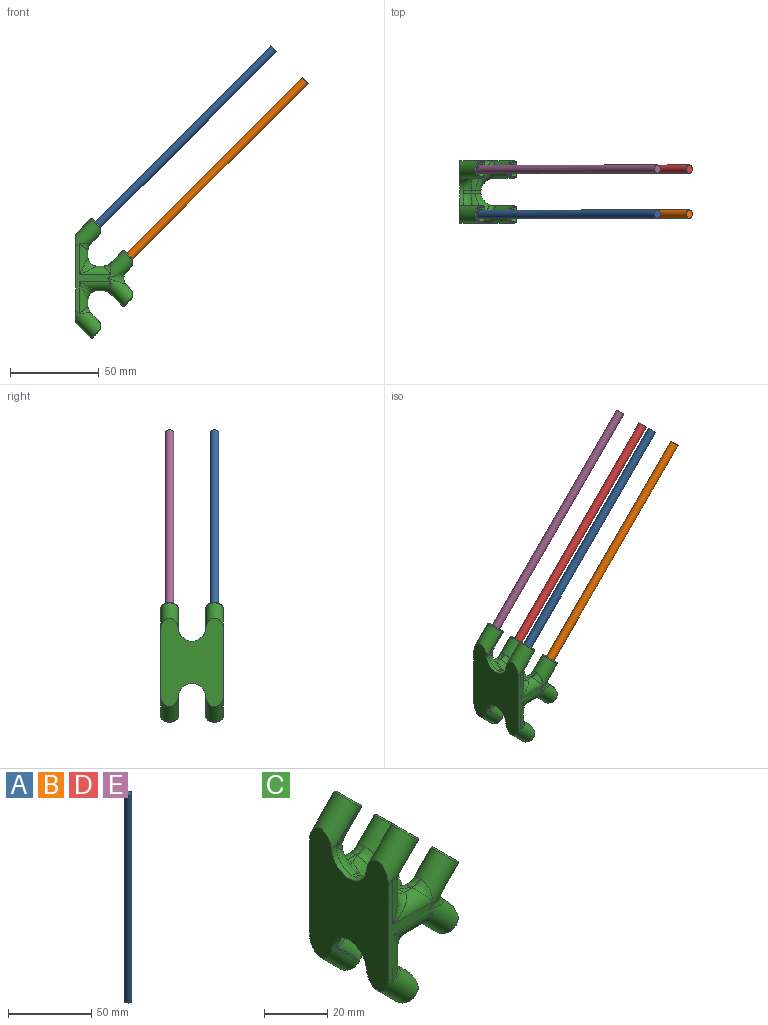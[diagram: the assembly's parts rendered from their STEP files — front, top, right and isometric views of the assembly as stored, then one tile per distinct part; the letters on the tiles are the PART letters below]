
ASSEMBLY  parts=5 mates=4
PART A: 3 faces, bbox 4.8x4.8x152.4 mm
  f0: cylinder r=2.38mm len=152.4mm, axis (0,0,-1), area 2280.2mm2, adj f1,f2
  f1: plane 4.76x4.76mm, normal (0,0,1), area 17.8mm2, adj f0
  f2: plane 4.76x4.76mm, normal (0,0,-1), area 17.8mm2, adj f0
PART B: same geometry as A
PART C: 244 faces, bbox 38.2x36.7x68.6 mm
  f0: plane 4.07x3.54mm, normal (1,0,0), area 7.5mm2, adj f104,f108,f122,f124,f168,f227,f243
  f1: plane 4.07x3.54mm, normal (1,0,0), area 7.5mm2, adj f106,f109,f121,f123,f170,f216,f240
  f2: plane 4.07x3.54mm, normal (1,0,0), area 7.5mm2, adj f80,f84,f98,f100,f164,f204,f236
  f3: plane 4.07x3.54mm, normal (1,0,0), area 7.5mm2, adj f82,f85,f97,f99,f166,f210,f239
  f4: cylinder r=5mm len=19.22mm, axis (0.71,0,0.71), area 376.4mm2, adj f10,f20,f43,f47,f57,f58,f62,f63
  f5: cylinder r=5mm len=19.22mm, axis (0.71,0,0.71), area 365.8mm2, adj f11,f21,f44,f48,f56,f58,f59,f60
  f6: cylinder r=2.59mm len=11.08mm, axis (0.71,0,0.71), area 157.5mm2, adj f8,f54,f181,f182,f183,f184
  f7: cylinder r=2.59mm len=11.08mm, axis (0.71,0,0.71), area 157.5mm2, adj f9,f55,f199,f200,f201,f202
  f8: bspline ~8.17x5.5mm, area 36.8mm2, adj f6,f11,f46,f153,f180,f185
  f9: bspline ~8.17x5.5mm, area 36.8mm2, adj f7,f10,f45,f152,f198,f203
  f10: plane 4.07x3.54mm, normal (1,0,0), area 7.5mm2, adj f4,f9,f45,f57,f161,f198,f235
  f11: plane 4.07x3.54mm, normal (1,0,0), area 7.5mm2, adj f5,f8,f46,f56,f163,f180,f233
  f12: cylinder r=5mm len=19.22mm, axis (0.71,0,0.71), area 315.1mm2, adj f18,f20,f25,f29,f39,f68,f69,f70
  f13: cylinder r=5mm len=19.22mm, axis (0.71,0,0.71), area 326.7mm2, adj f19,f21,f26,f30,f38,f65,f66,f67
  f14: cylinder r=2.59mm len=11.08mm, axis (0.71,0,0.71), area 157.5mm2, adj f16,f36,f193,f194,f195,f196
  f15: cylinder r=2.59mm len=11.08mm, axis (0.71,0,0.71), area 157.5mm2, adj f17,f37,f187,f188,f189,f190
  f16: bspline ~8.17x5.5mm, area 36.8mm2, adj f14,f19,f28,f155,f192,f197
  f17: bspline ~8.17x5.5mm, area 36.8mm2, adj f15,f18,f27,f154,f186,f191
  f18: plane 4.07x3.54mm, normal (1,0,0), area 7.5mm2, adj f12,f17,f27,f39,f157,f186,f229
  f19: plane 4.07x3.54mm, normal (1,0,0), area 7.5mm2, adj f13,f16,f28,f38,f159,f197,f231
  f20: plane 39.82x19.91mm, normal (0,-1,0), area 139.9mm2, adj f4,f12,f34,f52,f58,f80,f91,f104
  f21: plane 39.82x19.91mm, normal (0,1,0), area 139.9mm2, adj f5,f13,f35,f53,f58,f82,f92,f106
  f22: plane 3.84x2.56mm, normal (0,0,1), area 5.5mm2, adj f33,f35,f66,f72
  f23: plane 3.84x2.56mm, normal (0,0,1), area 5.5mm2, adj f31,f34,f69,f76
  f24: cylinder r=7.7mm len=15.4mm, axis (0,0,-1), area 91mm2, adj f25,f26,f29,f30,f31,f32,f33,f81
  f25: bspline ~7.95x7.08mm, area 1.1mm2, adj f12,f24,f145
  f26: bspline ~7.95x7.08mm, area 1.1mm2, adj f13,f24,f147
  f27: plane 9.02x4.73mm, normal (0.71,0,0.71), area 7.4mm2, adj f17,f18,f39,f154
  f28: plane 9.02x4.73mm, normal (0.71,0,0.71), area 7.4mm2, adj f16,f19,f38,f155
  f29: plane 10.18x10.18mm, normal (0,1,0), area 5.3mm2, adj f12,f24,f31,f70
  f30: plane 10.18x10.18mm, normal (0,-1,0), area 5.3mm2, adj f13,f24,f33,f65
  f31: torus R=12.7mm, axis (0,0,1), area 73.6mm2, adj f23,f24,f29,f32,f70,f75
  f32: bspline ~5.17x5.09mm, area 8.8mm2, adj f24,f31,f33,f74
  f33: torus R=12.7mm, axis (0,0,1), area 73.6mm2, adj f22,f24,f30,f32,f65,f73
  f34: cylinder r=5mm len=17.96mm, axis (1,0,0), area 74.8mm2, adj f20,f23,f68,f77
  f35: cylinder r=5mm len=17.96mm, axis (1,0,0), area 74.8mm2, adj f21,f22,f67,f71
  f36: plane 5.18x3.66mm, normal (0.71,0,0.71), area 21mm2, adj f14
  f37: plane 5.18x3.66mm, normal (0.71,0,0.71), area 21mm2, adj f15
  f38: torus R=4.5mm, axis (-0.71,0,-0.71), area 15.7mm2, adj f13,f19,f28,f155
  f39: torus R=4.5mm, axis (-0.71,0,-0.71), area 15.7mm2, adj f12,f18,f27,f154
  f40: plane 3.84x2.56mm, normal (1,0,0), area 5.5mm2, adj f51,f53,f60,f72
  f41: plane 3.84x2.56mm, normal (1,0,0), area 5.5mm2, adj f49,f52,f63,f76
  f42: cylinder r=7.7mm len=15.4mm, axis (-1,0,0), area 45.5mm2, adj f43,f44,f47,f48,f49,f50,f51,f58
  f43: bspline ~7.95x7.08mm, area 2.2mm2, adj f4,f42,f58
  f44: bspline ~7.95x7.08mm, area 2.2mm2, adj f5,f42,f58
  f45: plane 9.02x4.7mm, normal (0.71,0,0.71), area 7.4mm2, adj f9,f10,f57,f152
  f46: plane 9.02x4.7mm, normal (0.71,0,0.71), area 7.4mm2, adj f8,f11,f56,f153
  f47: plane 10.04x10.04mm, normal (0,1,0), area 5.3mm2, adj f4,f42,f49,f62
  f48: plane 10.04x10.04mm, normal (0,-1,0), area 5.3mm2, adj f5,f42,f51,f61
  f49: torus R=12.7mm, axis (1,0,0), area 73.6mm2, adj f41,f42,f47,f50,f62,f75
  f50: bspline ~5.17x5.09mm, area 8.8mm2, adj f42,f49,f51,f74
  f51: torus R=12.7mm, axis (1,0,0), area 73.6mm2, adj f40,f42,f48,f50,f61,f73
  f52: cylinder r=5mm len=17.96mm, axis (0,0,1), area 74.8mm2, adj f20,f41,f64,f77
  f53: cylinder r=5mm len=17.96mm, axis (0,0,1), area 74.8mm2, adj f21,f40,f59,f71
  f54: plane 5.18x3.66mm, normal (0.71,0,0.71), area 21mm2, adj f6
  f55: plane 5.18x3.66mm, normal (0.71,0,0.71), area 21mm2, adj f7
  f56: torus R=4.5mm, axis (-0.71,0,-0.71), area 15.7mm2, adj f5,f11,f46,f153
  f57: torus R=4.5mm, axis (-0.71,0,-0.71), area 15.7mm2, adj f4,f10,f45,f152
  f58: plane 50.18x35.52mm, normal (-1,0,0), area 1358.1mm2, adj f4,f5,f20,f21,f42,f43,f44,f103
  f59: bspline ~6.46x5.65mm, area 12.6mm2, adj f5,f53,f60
  f60: bspline ~3.55x1.47mm, area 1.7mm2, adj f5,f40,f59,f61
  f61: bspline ~15.45x9.76mm, area 29.5mm2, adj f5,f48,f51,f60
  f62: bspline ~15.45x9.76mm, area 29.5mm2, adj f4,f47,f49,f63
  f63: bspline ~3.55x1.47mm, area 1.7mm2, adj f4,f41,f62,f64
  f64: bspline ~6.46x5.16mm, area 12.6mm2, adj f4,f52,f63
  f65: bspline ~15.45x9.76mm, area 30mm2, adj f13,f30,f33,f66
  f66: bspline ~3.69x3.48mm, area 1.7mm2, adj f13,f22,f65,f67
  f67: bspline ~6.46x5.65mm, area 12.6mm2, adj f13,f35,f66
  f68: bspline ~6.46x5.16mm, area 12.6mm2, adj f12,f34,f69
  f69: bspline ~3.69x2.17mm, area 1.7mm2, adj f12,f23,f68,f70
  f70: bspline ~15.45x9.76mm, area 30mm2, adj f12,f29,f31,f69
  f71: bspline ~10x10mm, area 26.4mm2, adj f35,f53,f72
  f72: cylinder r=5mm len=5mm, axis (0,1,0), area 20.1mm2, adj f22,f40,f71,f73
  f73: bspline ~11.92x5.76mm, area 48.2mm2, adj f33,f51,f72,f74
  f74: bspline ~3.96x2.6mm, area 6.8mm2, adj f32,f50,f73,f75
  f75: bspline ~11.92x5.76mm, area 48.2mm2, adj f31,f49,f74,f76
  f76: cylinder r=5mm len=5mm, axis (0,1,0), area 20.1mm2, adj f23,f41,f75,f77
  f77: bspline ~10x10mm, area 26.4mm2, adj f34,f52,f76
  f78: plane 3.84x2.56mm, normal (0,0,-1), area 5.5mm2, adj f90,f92,f132,f138
  f79: plane 3.84x2.56mm, normal (0,0,-1), area 5.5mm2, adj f88,f91,f135,f142
  f80: cylinder r=5mm len=19.22mm, axis (0.71,0,-0.71), area 325.9mm2, adj f2,f20,f81,f86,f100,f134,f135,f136
  f81: bspline ~2.42x1.81mm, area 1.1mm2, adj f24,f80,f145
  f82: cylinder r=5mm len=19.22mm, axis (0.71,0,-0.71), area 315.3mm2, adj f3,f21,f83,f87,f99,f131,f132,f133
  f83: bspline ~2.42x1.81mm, area 1.1mm2, adj f24,f82,f147
  f84: plane 9.02x4.7mm, normal (0.71,0,-0.71), area 7.4mm2, adj f2,f98,f100,f150
  f85: plane 9.02x4.7mm, normal (0.71,0,-0.71), area 7.4mm2, adj f3,f97,f99,f151
  f86: plane 10.04x10.04mm, normal (0,1,0), area 5.3mm2, adj f24,f80,f88,f136
  f87: plane 10.04x10.04mm, normal (0,-1,0), area 5.3mm2, adj f24,f82,f90,f131
  f88: torus R=12.7mm, axis (0,0,-1), area 73.6mm2, adj f24,f79,f86,f89,f136,f141
  f89: bspline ~5.17x5.09mm, area 8.8mm2, adj f24,f88,f90,f140
  f90: torus R=12.7mm, axis (0,0,-1), area 73.6mm2, adj f24,f78,f87,f89,f131,f139
  f91: cylinder r=5mm len=17.96mm, axis (1,0,0), area 74.8mm2, adj f20,f79,f134,f143
  f92: cylinder r=5mm len=17.96mm, axis (1,0,0), area 74.8mm2, adj f21,f78,f133,f137
  f93: cylinder r=2.59mm len=11.08mm, axis (0.71,0,-0.71), area 157.5mm2, adj f94,f97,f211,f212,f213,f214
  f94: plane 5.18x3.66mm, normal (0.71,0,-0.71), area 21mm2, adj f93
  f95: cylinder r=2.59mm len=11.08mm, axis (0.71,0,-0.71), area 157.5mm2, adj f96,f98,f205,f206,f207,f208
  f96: plane 5.18x3.66mm, normal (0.71,0,-0.71), area 21mm2, adj f95
  f97: bspline ~8.17x5.5mm, area 36.8mm2, adj f3,f85,f93,f151,f210,f215
  f98: bspline ~8.17x5.5mm, area 36.8mm2, adj f2,f84,f95,f150,f204,f209
  f99: torus R=4.5mm, axis (-0.71,0,0.71), area 15.7mm2, adj f3,f82,f85,f151
  f100: torus R=4.5mm, axis (-0.71,0,0.71), area 15.7mm2, adj f2,f80,f84,f150
  f101: plane 3.84x2.56mm, normal (1,0,0), area 5.5mm2, adj f114,f116,f126,f138
  f102: plane 3.84x2.56mm, normal (1,0,0), area 5.5mm2, adj f112,f115,f129,f142
  f103: cylinder r=7.7mm len=15.4mm, axis (-1,0,0), area 45.5mm2, adj f58,f105,f107,f110,f111,f112,f113,f114
  f104: cylinder r=5mm len=19.22mm, axis (0.71,0,-0.71), area 365.7mm2, adj f0,f20,f58,f105,f110,f124,f128,f129
  f105: bspline ~7.95x7.08mm, area 2.2mm2, adj f58,f103,f104
  f106: cylinder r=5mm len=19.22mm, axis (0.71,0,-0.71), area 377.3mm2, adj f1,f21,f58,f107,f111,f123,f125,f126
  f107: bspline ~7.95x7.08mm, area 2.2mm2, adj f58,f103,f106
  f108: plane 9.02x4.73mm, normal (0.71,0,-0.71), area 7.4mm2, adj f0,f122,f124,f148
  f109: plane 9.02x4.73mm, normal (0.71,0,-0.71), area 7.4mm2, adj f1,f121,f123,f149
  f110: plane 10.17x10.17mm, normal (0,1,0), area 5.3mm2, adj f103,f104,f112,f128
  f111: plane 10.17x10.17mm, normal (0,-1,0), area 5.3mm2, adj f103,f106,f114,f127
  f112: torus R=12.7mm, axis (1,0,0), area 73.6mm2, adj f102,f103,f110,f113,f128,f141
  f113: bspline ~5.17x5.09mm, area 8.8mm2, adj f103,f112,f114,f140
  f114: torus R=12.7mm, axis (1,0,0), area 73.6mm2, adj f101,f103,f111,f113,f127,f139
  f115: cylinder r=5mm len=17.96mm, axis (0,0,-1), area 74.8mm2, adj f20,f102,f130,f143
  f116: cylinder r=5mm len=17.96mm, axis (0,0,-1), area 74.8mm2, adj f21,f101,f125,f137
  f117: cylinder r=2.59mm len=11.08mm, axis (0.71,0,-0.71), area 157.5mm2, adj f118,f121,f217,f218,f219,f220
  f118: plane 5.18x3.66mm, normal (0.71,0,-0.71), area 21mm2, adj f117
  f119: cylinder r=2.59mm len=11.08mm, axis (0.71,0,-0.71), area 157.5mm2, adj f120,f122,f223,f224,f225,f226
  f120: plane 5.18x3.66mm, normal (0.71,0,-0.71), area 21mm2, adj f119
  f121: bspline ~8.17x5.5mm, area 36.8mm2, adj f1,f109,f117,f149,f216,f221
  f122: bspline ~8.17x5.5mm, area 36.8mm2, adj f0,f108,f119,f148,f222,f227
  f123: torus R=4.5mm, axis (-0.71,0,0.71), area 15.7mm2, adj f1,f106,f109,f149
  f124: torus R=4.5mm, axis (-0.71,0,0.71), area 15.7mm2, adj f0,f104,f108,f148
  f125: bspline ~6.46x5.65mm, area 12.6mm2, adj f106,f116,f126
  f126: bspline ~3.69x2.17mm, area 1.7mm2, adj f101,f106,f125,f127
  f127: bspline ~15.45x9.76mm, area 30.1mm2, adj f106,f111,f114,f126
  f128: bspline ~15.45x9.76mm, area 30.1mm2, adj f104,f110,f112,f129
  f129: bspline ~3.55x1.47mm, area 1.7mm2, adj f102,f104,f128,f130
  f130: bspline ~6.46x5.16mm, area 12.6mm2, adj f104,f115,f129
  f131: bspline ~15.45x9.76mm, area 29.5mm2, adj f82,f87,f90,f132
  f132: bspline ~3.69x3.48mm, area 1.7mm2, adj f78,f82,f131,f133
  f133: bspline ~6.46x5.65mm, area 12.6mm2, adj f82,f92,f132
  f134: bspline ~6.46x5.16mm, area 12.6mm2, adj f80,f91,f135
  f135: bspline ~3.69x2.17mm, area 1.7mm2, adj f79,f80,f134,f136
  f136: bspline ~15.45x9.76mm, area 29.5mm2, adj f80,f86,f88,f135
  f137: bspline ~10x10mm, area 26.4mm2, adj f92,f116,f138
  f138: cylinder r=5mm len=5mm, axis (0,1,0), area 20.1mm2, adj f78,f101,f137,f139
  f139: bspline ~11.92x5.76mm, area 48.2mm2, adj f90,f114,f138,f140
  f140: bspline ~3.96x2.6mm, area 6.8mm2, adj f89,f113,f139,f141
  f141: bspline ~11.92x5.76mm, area 48.2mm2, adj f88,f112,f140,f142
  f142: cylinder r=5mm len=5mm, axis (0,1,0), area 20.1mm2, adj f79,f102,f141,f143
  f143: bspline ~10x10mm, area 26.4mm2, adj f91,f115,f142
  f144: bspline ~10.6x9.86mm, area 92.4mm2, adj f12,f80,f145
  f145: bspline ~3.02x2.71mm, area 1mm2, adj f25,f81,f144
  f146: bspline ~10.6x9.86mm, area 92.4mm2, adj f13,f82,f147
  f147: bspline ~3.02x2.71mm, area 1mm2, adj f26,f83,f146
  f148: plane 4.07x3.54mm, normal (1,0,0), area 7.5mm2, adj f104,f108,f122,f124,f169,f222,f242
  f149: plane 4.07x3.54mm, normal (1,0,0), area 7.5mm2, adj f106,f109,f121,f123,f171,f221,f241
  f150: plane 4.07x3.54mm, normal (1,0,0), area 7.5mm2, adj f80,f84,f98,f100,f165,f209,f237
  f151: plane 4.07x3.54mm, normal (1,0,0), area 7.5mm2, adj f82,f85,f97,f99,f167,f215,f238
  f152: plane 4.07x3.54mm, normal (1,0,0), area 7.5mm2, adj f4,f9,f45,f57,f160,f203,f234
  f153: plane 4.07x3.54mm, normal (1,0,0), area 7.5mm2, adj f5,f8,f46,f56,f162,f185,f232
  f154: plane 4.07x3.54mm, normal (1,0,0), area 7.5mm2, adj f12,f17,f27,f39,f156,f191,f228
  f155: plane 4.07x3.54mm, normal (1,0,0), area 7.5mm2, adj f13,f16,f28,f38,f158,f192,f230
  f156: plane 3.07x2.67mm, normal (0,-1,0), area 4.5mm2, adj f154,f179,f190,f191,f228
  f157: plane 3.07x2.67mm, normal (0,1,0), area 4.5mm2, adj f18,f179,f186,f187,f229
  f158: plane 3.07x2.67mm, normal (0,-1,0), area 4.5mm2, adj f155,f178,f192,f193,f230
  f159: plane 3.07x2.67mm, normal (0,1,0), area 4.5mm2, adj f19,f178,f196,f197,f231
  f160: plane 3.07x2.67mm, normal (0,-1,0), area 4.5mm2, adj f152,f176,f202,f203,f234
  f161: plane 3.07x2.67mm, normal (0,1,0), area 4.5mm2, adj f10,f176,f198,f199,f235
  f162: plane 3.07x2.67mm, normal (0,-1,0), area 4.5mm2, adj f153,f177,f184,f185,f232
  f163: plane 3.07x2.67mm, normal (0,1,0), area 4.5mm2, adj f11,f177,f180,f181,f233
  f164: plane 3.07x2.67mm, normal (0,-1,0), area 4.5mm2, adj f2,f175,f204,f205,f236
  f165: plane 3.07x2.67mm, normal (0,1,0), area 4.5mm2, adj f150,f175,f208,f209,f237
  f166: plane 3.07x2.67mm, normal (0,-1,0), area 4.5mm2, adj f3,f174,f210,f211,f239
  f167: plane 3.07x2.67mm, normal (0,1,0), area 4.5mm2, adj f151,f174,f214,f215,f238
  f168: plane 3.07x2.67mm, normal (0,-1,0), area 4.5mm2, adj f0,f172,f226,f227,f243
  f169: plane 3.07x2.67mm, normal (0,1,0), area 4.5mm2, adj f148,f172,f222,f223,f242
  f170: plane 3.07x2.67mm, normal (0,-1,0), area 4.5mm2, adj f1,f173,f216,f217,f240
  f171: plane 3.07x2.67mm, normal (0,1,0), area 4.5mm2, adj f149,f173,f220,f221,f241
  f172: cylinder r=1.25mm len=3.25mm, axis (-1,0,0), area 8.4mm2, adj f168,f169,f224,f225,f242,f243
  f173: cylinder r=1.25mm len=3.25mm, axis (-1,0,0), area 8.4mm2, adj f170,f171,f218,f219,f240,f241
  f174: cylinder r=1.25mm len=3.25mm, axis (-1,0,0), area 8.4mm2, adj f166,f167,f212,f213,f238,f239
  f175: cylinder r=1.25mm len=3.25mm, axis (-1,0,0), area 8.4mm2, adj f164,f165,f206,f207,f236,f237
  f176: cylinder r=1.25mm len=3.25mm, axis (-1,0,0), area 8.4mm2, adj f160,f161,f200,f201,f234,f235
  f177: cylinder r=1.25mm len=3.25mm, axis (-1,0,0), area 8.4mm2, adj f162,f163,f182,f183,f232,f233
  f178: cylinder r=1.25mm len=3.25mm, axis (-1,0,0), area 8.4mm2, adj f158,f159,f194,f195,f230,f231
  f179: cylinder r=1.25mm len=3.25mm, axis (-1,0,0), area 8.4mm2, adj f156,f157,f188,f189,f228,f229
  f180: bspline ~1.1x0.82mm, area 0.5mm2, adj f8,f11,f163,f181
  f181: cylinder r=0.5mm len=2.59mm, axis (0.71,0,0.71), area 1.6mm2, adj f6,f163,f180,f182
  f182: bspline ~2.22x1.94mm, area 1mm2, adj f6,f177,f181,f183
  f183: bspline ~2.22x1.94mm, area 1mm2, adj f6,f177,f182,f184
  f184: cylinder r=0.5mm len=2.59mm, axis (0.71,0,0.71), area 1.6mm2, adj f6,f162,f183,f185
  f185: bspline ~1.43x0.9mm, area 0.5mm2, adj f8,f153,f162,f184
  f186: bspline ~1.1x0.82mm, area 0.5mm2, adj f17,f18,f157,f187
  f187: cylinder r=0.5mm len=2.59mm, axis (0.71,0,0.71), area 1.6mm2, adj f15,f157,f186,f188
  f188: bspline ~2.22x1.94mm, area 1mm2, adj f15,f179,f187,f189
  f189: bspline ~2.22x1.94mm, area 1mm2, adj f15,f179,f188,f190
  f190: cylinder r=0.5mm len=2.59mm, axis (0.71,0,0.71), area 1.6mm2, adj f15,f156,f189,f191
  f191: bspline ~1.69x1.16mm, area 0.5mm2, adj f17,f154,f156,f190
  f192: bspline ~1.69x1.16mm, area 0.5mm2, adj f16,f155,f158,f193
  f193: cylinder r=0.5mm len=2.59mm, axis (0.71,0,0.71), area 1.6mm2, adj f14,f158,f192,f194
  f194: bspline ~2.22x1.94mm, area 1mm2, adj f14,f178,f193,f195
  f195: bspline ~2.22x1.94mm, area 1mm2, adj f14,f178,f194,f196
  f196: cylinder r=0.5mm len=2.59mm, axis (0.71,0,0.71), area 1.6mm2, adj f14,f159,f195,f197
  f197: bspline ~1.69x1.16mm, area 0.5mm2, adj f16,f19,f159,f196
  f198: bspline ~1.1x0.82mm, area 0.5mm2, adj f9,f10,f161,f199
  f199: cylinder r=0.5mm len=2.59mm, axis (0.71,0,0.71), area 1.6mm2, adj f7,f161,f198,f200
  f200: bspline ~2.22x1.94mm, area 1mm2, adj f7,f176,f199,f201
  f201: bspline ~2.22x1.94mm, area 1mm2, adj f7,f176,f200,f202
  f202: cylinder r=0.5mm len=2.59mm, axis (0.71,0,0.71), area 1.6mm2, adj f7,f160,f201,f203
  f203: bspline ~1.43x0.9mm, area 0.5mm2, adj f9,f152,f160,f202
  f204: bspline ~1.1x0.82mm, area 0.5mm2, adj f2,f98,f164,f205
  f205: cylinder r=0.5mm len=2.59mm, axis (0.71,0,-0.71), area 1.6mm2, adj f95,f164,f204,f206
  f206: bspline ~2.22x1.94mm, area 1mm2, adj f95,f175,f205,f207
  f207: bspline ~2.22x1.94mm, area 1mm2, adj f95,f175,f206,f208
  f208: cylinder r=0.5mm len=2.59mm, axis (0.71,0,-0.71), area 1.6mm2, adj f95,f165,f207,f209
  f209: bspline ~1.69x1.16mm, area 0.5mm2, adj f98,f150,f165,f208
  f210: bspline ~1.69x1.16mm, area 0.5mm2, adj f3,f97,f166,f211
  f211: cylinder r=0.5mm len=2.59mm, axis (0.71,0,-0.71), area 1.6mm2, adj f93,f166,f210,f212
  f212: bspline ~2.22x1.94mm, area 1mm2, adj f93,f174,f211,f213
  f213: bspline ~2.22x1.94mm, area 1mm2, adj f93,f174,f212,f214
  f214: cylinder r=0.5mm len=2.59mm, axis (0.71,0,-0.71), area 1.6mm2, adj f93,f167,f213,f215
  f215: bspline ~1.69x1.16mm, area 0.5mm2, adj f97,f151,f167,f214
  f216: bspline ~1.1x0.82mm, area 0.5mm2, adj f1,f121,f170,f217
  f217: cylinder r=0.5mm len=2.59mm, axis (0.71,0,-0.71), area 1.6mm2, adj f117,f170,f216,f218
  f218: bspline ~2.22x1.94mm, area 1mm2, adj f117,f173,f217,f219
  f219: bspline ~2.22x1.94mm, area 1mm2, adj f117,f173,f218,f220
  f220: cylinder r=0.5mm len=2.59mm, axis (0.71,0,-0.71), area 1.6mm2, adj f117,f171,f219,f221
  f221: bspline ~1.69x1.16mm, area 0.5mm2, adj f121,f149,f171,f220
  f222: bspline ~1.69x1.16mm, area 0.5mm2, adj f122,f148,f169,f223
  f223: cylinder r=0.5mm len=2.59mm, axis (0.71,0,-0.71), area 1.6mm2, adj f119,f169,f222,f224
  f224: bspline ~2.22x1.94mm, area 1mm2, adj f119,f172,f223,f225
  f225: bspline ~2.22x1.94mm, area 1mm2, adj f119,f172,f224,f226
  f226: cylinder r=0.5mm len=2.59mm, axis (0.71,0,-0.71), area 1.6mm2, adj f119,f168,f225,f227
  f227: bspline ~1.69x1.16mm, area 0.5mm2, adj f0,f122,f168,f226
  f228: bspline ~2.73x2.58mm, area 3.5mm2, adj f12,f154,f156,f179,f229
  f229: bspline ~2.65x2.45mm, area 3.5mm2, adj f12,f18,f157,f179,f228
  f230: bspline ~2.73x2.58mm, area 3.5mm2, adj f13,f155,f158,f178,f231
  f231: bspline ~2.65x2.45mm, area 3.5mm2, adj f13,f19,f159,f178,f230
  f232: bspline ~2.73x2.58mm, area 3.5mm2, adj f5,f153,f162,f177,f233
  f233: bspline ~2.65x2.45mm, area 3.5mm2, adj f5,f11,f163,f177,f232
  f234: bspline ~2.73x2.58mm, area 3.5mm2, adj f4,f152,f160,f176,f235
  f235: bspline ~2.65x2.45mm, area 3.5mm2, adj f4,f10,f161,f176,f234
  f236: bspline ~2.65x2.45mm, area 3.5mm2, adj f2,f80,f164,f175,f237
  f237: bspline ~2.73x2.58mm, area 3.5mm2, adj f80,f150,f165,f175,f236
  f238: bspline ~2.73x2.58mm, area 3.5mm2, adj f82,f151,f167,f174,f239
  f239: bspline ~2.65x2.45mm, area 3.5mm2, adj f3,f82,f166,f174,f238
  f240: bspline ~2.65x2.45mm, area 3.5mm2, adj f1,f106,f170,f173,f241
  f241: bspline ~2.73x2.58mm, area 3.5mm2, adj f106,f149,f171,f173,f240
  f242: bspline ~2.73x2.58mm, area 3.5mm2, adj f104,f148,f169,f172,f243
  f243: bspline ~2.65x2.45mm, area 3.5mm2, adj f0,f104,f168,f172,f242
PART D: same geometry as A
PART E: same geometry as A
PLACE A rot(axis=(0.92,0,-0.38),180deg) t=(111.78,-14.71,132.79)mm
PLACE B rot(axis=(0.92,0,-0.38),180deg) t=(129.74,-14.71,114.83)mm
PLACE C at identity
PLACE D rot(axis=(0.92,0,-0.38),180deg) t=(129.74,10.69,114.83)mm
PLACE E rot(axis=(0.92,0,-0.38),180deg) t=(111.78,10.69,132.79)mm
MATE revolute B.f0 <-> C.f15  axis (-0.71,0,-0.71) through (21.98,-14.71,7.07)mm
MATE revolute D.f0 <-> C.f14  axis (-0.71,0,-0.71) through (21.98,10.69,7.07)mm
MATE revolute E.f0 <-> C.f5  axis (-0.71,0,-0.71) through (4.02,10.69,25.03)mm
MATE revolute A.f0 <-> C.f4  axis (-0.71,0,-0.71) through (4.02,-14.71,25.03)mm
